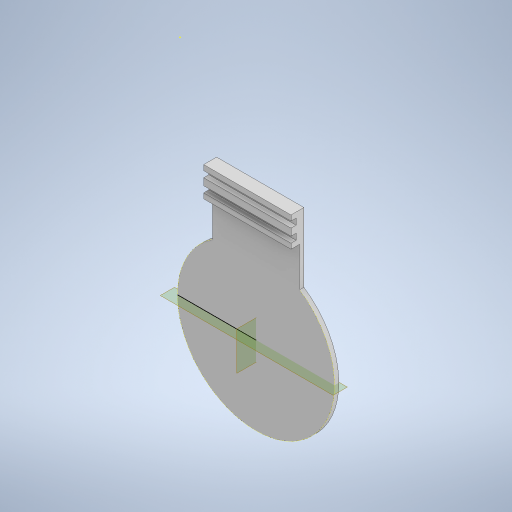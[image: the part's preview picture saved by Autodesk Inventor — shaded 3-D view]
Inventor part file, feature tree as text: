
AUTODESK INVENTOR PART (.ipt)
format: ipt  version: 2023 (Build 270158000, 158)  size: 498,176 bytes
history: native  units: mm
features: sketch x7, other x7, extrude x6, projected_geometry x1
ambient origin geometry x8: Origin, YZ Plane, XZ Plane, XY Plane, X Axis, Y Axis, Z Axis, Center Point
bodies: Solide1 (feature_tree)
feature tree (21):
  extrude  "Extrusion1"  Depth=0.5mm
  extrude  "Extrusion12"  Depth=50.0mm
  extrude  "Extrusion21"  Depth=3.0mm
  extrude  "Extrusion22"  Depth=3.0mm
  extrude  "Extrusion23"  Depth=2.9mm TaperAngle=0.0deg
  extrude  "Extrusion24"  Depth=2.0mm TaperAngle=0.0deg
  sketch  "Esquisse28"
  other  "Plan de construction5"
  other  "Plan de construction6"
  sketch  "Esquisse1"
  other  "Référence1"
  other  "Référence2"
  sketch  "Esquisse13"
  sketch  "Esquisse24"
  sketch  "Esquisse25"
  sketch  "Esquisse26"
  sketch  "Esquisse27"
  projected_geometry  "Boucle projetée10"
  other  "<userpath>\Desktop\PE-SM\3D\Ensemble.iam"
  other  "Ensemble.iam"
  other  "PE:1"
